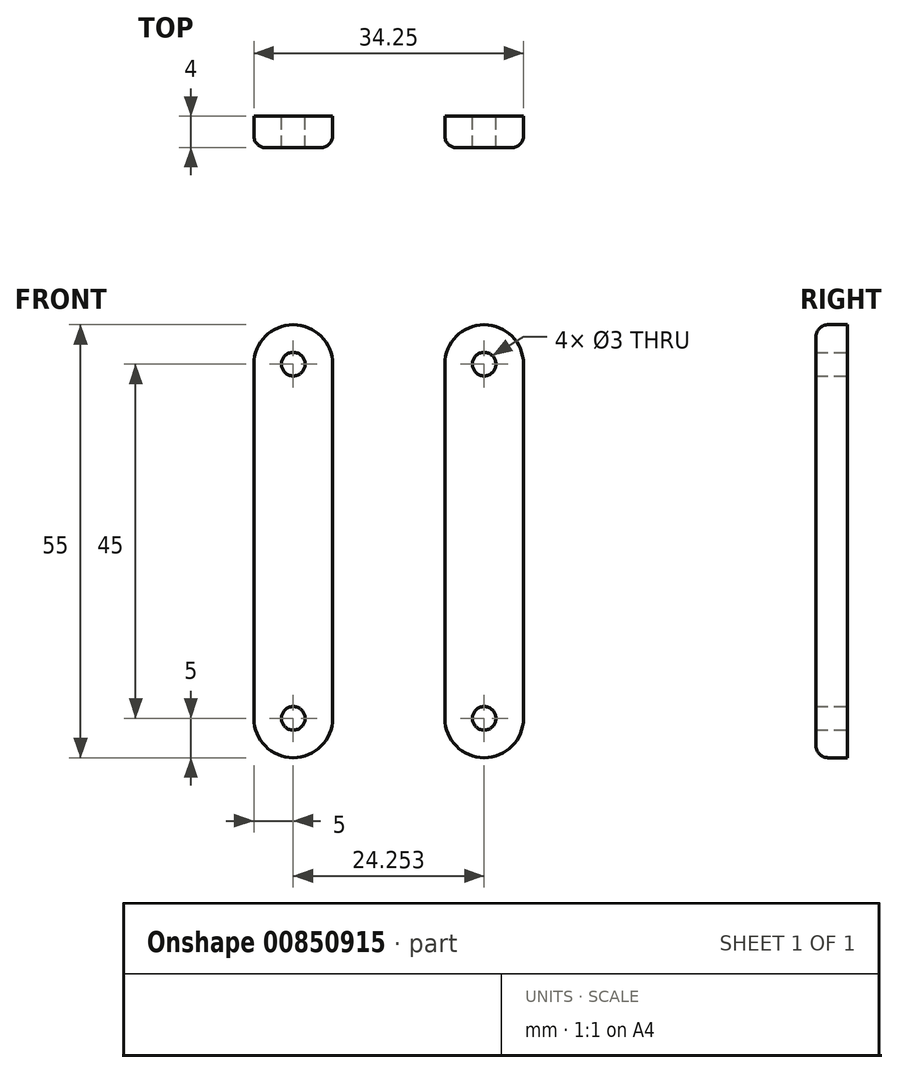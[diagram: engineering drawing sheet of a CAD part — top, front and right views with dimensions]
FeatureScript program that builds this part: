
annotation { "Feature Type Name" : "Feature", "Feature Type Description" : "" }
export const myFeature = defineFeature(function(context is Context, id is Id, definition is map)
    precondition{}
    {
        {
            var Q0;
            Q0=qCreatedBy(makeId("Front.planeOp"),FACE);
            var sketch = newSketch(context, id + "F0", { "sketchPlane" : qUnion([Q0])});
            skLineSegment(sketch, "E0.bottom", {"start": v(0, 55) * mm, "end": v(10, 55) * mm});
            skLineSegment(sketch, "E0.top", {"start": v(0, 0) * mm, "end": v(10, 0) * mm});
            skLineSegment(sketch, "E0.left", {"start": v(0, 55) * mm, "end": v(0, 0) * mm});
            skLineSegment(sketch, "E0.right", {"start": v(10, 55) * mm, "end": v(10, 0) * mm});
            skLineSegment(sketch, "E1.bottom", {"start": v(24.25, 55) * mm, "end": v(34.25, 55) * mm});
            skLineSegment(sketch, "E1.top", {"start": v(24.25, 0) * mm, "end": v(34.25, 0) * mm});
            skLineSegment(sketch, "E1.left", {"start": v(24.25, 55) * mm, "end": v(24.25, 0) * mm});
            skLineSegment(sketch, "E1.right", {"start": v(34.25, 55) * mm, "end": v(34.25, 0) * mm});
            skPoint(sketch, "E2", {"position": v(5, 50) * mm});
            skPoint(sketch, "E3", {"position": v(29.25, 50) * mm});
            skPoint(sketch, "E4", {"position": v(5, 5) * mm});
            skPoint(sketch, "E5", {"position": v(29.25, 5) * mm});
            skSolve(sketch);
        }
        {
            var Q0;
            Q0=makeQuery(id+"F0.imprint","IMPRINT",FACE,{"disambiguationData":[TD([[makeQuery(id+"F0.imprint","IMPRINT",EDGE,{"derivedFrom":sQuery(id+"F0.wireOp",EDGE,"E0.bottom")}),-1.0]])]});
            var Q1;
            Q1=makeQuery(id+"F0.imprint","IMPRINT",FACE,{"disambiguationData":[TD([[makeQuery(id+"F0.imprint","IMPRINT",EDGE,{"derivedFrom":sQuery(id+"F0.wireOp",EDGE,"E1.bottom")}),-1.0]])]});
            extrude(context, id + "F1", {"entities" : qUnion([Q0, Q1]), "depth" : 4 * mm, "offsetDistance" : 25 * mm});
        }
        {
            var Q0;
            Q0=qCreatedBy(makeId("Front.planeOp"),FACE);
            var sketch = newSketch(context, id + "F2", { "sketchPlane" : qUnion([Q0])});
            skPoint(sketch, "E6", {"position": v(5, 50) * mm});
            skPoint(sketch, "E7", {"position": v(29.25, 50) * mm});
            skPoint(sketch, "E8", {"position": v(29.25, 5) * mm});
            skPoint(sketch, "E9", {"position": v(5, 5) * mm});
            skSolve(sketch);
        }
        {
            var Q0;
            Q0=sQuery(id+"F2.wireOp",VERTEX,"E6");
            var Q1;
            Q1=sQuery(id+"F2.wireOp",VERTEX,"E7");
            var Q2;
            Q2=sQuery(id+"F2.wireOp",VERTEX,"E9");
            var Q3;
            Q3=sQuery(id+"F2.wireOp",VERTEX,"E8");
            var Q4;
            Q4=makeQuery(id+"F1.opExtrude","SWEPT_BODY",BODY,{"disambiguationData":[OSD([sQuery(id+"F0.wireOp",EDGE,"E0.bottom"),sQuery(id+"F0.wireOp",EDGE,"E0.top"),sQuery(id+"F0.wireOp",EDGE,"E0.left"),sQuery(id+"F0.wireOp",EDGE,"E0.right")])]});
            var Q5;
            Q5=makeQuery(id+"F1.opExtrude","SWEPT_BODY",BODY,{"disambiguationData":[OSD([sQuery(id+"F0.wireOp",EDGE,"E1.bottom"),sQuery(id+"F0.wireOp",EDGE,"E1.top"),sQuery(id+"F0.wireOp",EDGE,"E1.left"),sQuery(id+"F0.wireOp",EDGE,"E1.right")])]});
            hole(context, id + "F3", {"style" : HoleStyle.SIMPLE, "endStyle" : HoleEndStyle.THROUGH, "oppositeDirection" : true, "holeDiameter" : 3 * mm, "majorDiameter" : 5 * mm, "isTappedThrough" : true, "tappedDepth" : 12 * mm, "tapClearance" : 3, "locations" : qUnion([Q0, Q1, Q2, Q3]), "scope" : qUnion([Q4, Q5])});
        }
        {
            var Q0;
            Q0=makeQuery(id+"F1.opExtrude","SWEPT_EDGE",EDGE,{"disambiguationData":[OSD([sQuery(id+"F0.wireOp",EDGE,"E0.bottom"),sQuery(id+"F0.wireOp",EDGE,"E0.left")])]});
            var Q1;
            Q1=makeQuery(id+"F1.opExtrude","SWEPT_EDGE",EDGE,{"disambiguationData":[OSD([sQuery(id+"F0.wireOp",EDGE,"E1.bottom"),sQuery(id+"F0.wireOp",EDGE,"E1.left")])]});
            var Q2;
            Q2=makeQuery(id+"F1.opExtrude","SWEPT_EDGE",EDGE,{"disambiguationData":[OSD([sQuery(id+"F0.wireOp",EDGE,"E1.top"),sQuery(id+"F0.wireOp",EDGE,"E1.left")])]});
            var Q3;
            Q3=makeQuery(id+"F1.opExtrude","SWEPT_EDGE",EDGE,{"disambiguationData":[OSD([sQuery(id+"F0.wireOp",EDGE,"E0.top"),sQuery(id+"F0.wireOp",EDGE,"E0.left")])]});
            var Q4;
            Q4=makeQuery(id+"F1.opExtrude","SWEPT_EDGE",EDGE,{"disambiguationData":[OSD([sQuery(id+"F0.wireOp",EDGE,"E0.top"),sQuery(id+"F0.wireOp",EDGE,"E0.right")])]});
            var Q5;
            Q5=makeQuery(id+"F1.opExtrude","SWEPT_EDGE",EDGE,{"disambiguationData":[OSD([sQuery(id+"F0.wireOp",EDGE,"E1.top"),sQuery(id+"F0.wireOp",EDGE,"E1.right")])]});
            var Q6;
            Q6=makeQuery(id+"F1.opExtrude","SWEPT_EDGE",EDGE,{"disambiguationData":[OSD([sQuery(id+"F0.wireOp",EDGE,"E0.bottom"),sQuery(id+"F0.wireOp",EDGE,"E0.right")])]});
            var Q7;
            Q7=makeQuery(id+"F1.opExtrude","SWEPT_EDGE",EDGE,{"disambiguationData":[OSD([sQuery(id+"F0.wireOp",EDGE,"E1.bottom"),sQuery(id+"F0.wireOp",EDGE,"E1.right")])]});
            fillet(context, id + "F4", {"entities" : qUnion([Q0, Q1, Q2, Q3, Q4, Q5, Q6, Q7]), "radius" : 5 * mm, "tangentPropagation" : true, "allowEdgeOverflow" : false});
        }
        {
            var Q0;
            Q0=makeQuery(id+"F1.opExtrude","CAP_EDGE",EDGE,{"disambiguationData":[OSD([sQuery(id+"F0.wireOp",EDGE,"E0.left")])],"isStart":false});
            var Q1;
            Q1=makeQuery(id+"F1.opExtrude","CAP_EDGE",EDGE,{"disambiguationData":[OSD([sQuery(id+"F0.wireOp",EDGE,"E1.left")])],"isStart":false});
            fillet(context, id + "F5", {"entities" : qUnion([Q0, Q1]), "radius" : 1.5 * mm, "tangentPropagation" : true, "allowEdgeOverflow" : false});
        }
    });
